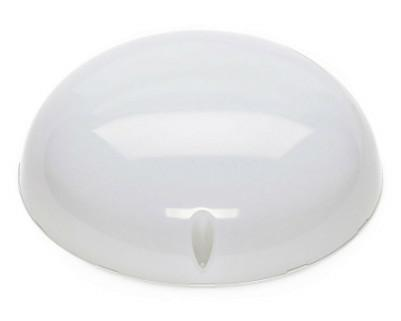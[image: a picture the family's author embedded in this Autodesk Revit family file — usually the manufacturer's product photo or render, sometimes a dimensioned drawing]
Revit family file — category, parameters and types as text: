
# Revit family: GALAD Находка LED
name_source: partatom
category: Осветительные приборы
revit_build: Autodesk Revit 2018 (Build: 20180423_1000(x64)
units: mm (PartAtom-declared; Revit-internal decimal feet)

## family parameters
Источник света = Да
Общий = Нет
Основа = Грань
При загрузке вырезать с полостями = Нет
Размер круглого соединителя = Использовать диаметр
Тип детали = Нормальный
Точка расчета площади = Нет

## types (1)
- GALAD Находка LED-9 ECO IP30
    ADSK_Версия Revit = 2018
    ADSK_Версия семейства = 1.01
    ADSK_Единица измерения = шт.
    ADSK_Классификация нагрузок = Освещение
    ADSK_Код изделия = 18158
    ADSK_Количество = 1
    ADSK_Количество фаз = 1
    ADSK_Коэффициент мощности = 0.95
    ADSK_Марка = GALAD Находка LED-9 ECO IP30
    ADSK_Масса = 0.2
    ADSK_Масса_Текст = 0.2
    ADSK_Наименование = GALAD Находка LED-9 ECO IP30
    ADSK_Наименование краткое = GALAD Находка LED-9 ECO IP30
    ADSK_Напряжение = 230 В
    ADSK_Номинальная мощность = 9 В·А
    ADSK_Обозначение = ГОСТ 15150-69
    ADSK_Полная мощность = 9 В·А
    ADSK_Размер_Высота = 53 мм
    ADSK_Размер_Длина = 174 мм
    ADSK_Размер_Ширина = 174 мм
    ADSK_Ток = 0 А
    ADSK_Энергоэффективность = 56 лм/Вт
    IP = 30
    URL = https://galad.ru
    Блок аварийного питания = Нет
    Видимая форма излучения при визуализации = Нет
    Возможный угол наклона = 0
    Группа модели = Светильники
    Диапазон цветовой температуры = 5028±283
    Изготовитель = АО «КАДОШКИНСКИЙ ЭЛЕКТРОТЕХНИЧЕСКИЙ ЗАВОД»
    Излучение по диаметру окружности = 610 мм
    Класс Защиты = 1
    Класс защиты от поражения электрическим током = 2
    Класс светораспределения = П
    Климатическая зона = УХЛ4
    Климатическое исполнение = 1…35 °С
    Коэффициент пульсации = менее 5%
    Материал корпуса = ПММА
    Материал рассеивателя = ПММА
    Неравномерность яркости = 0
    Область использования = ЖКХ
    Описание = Светодиодный светильник GALAD Находка LED укомплектован матовым рассеивателем для минимизации слепящего действия и встроенным блоком питания. Ударопрочное защитное стекло выполнено из светостабилизированного поликарбоната. Установка светильника возможна на стену или на потолок.
    Отметка по умолчанию = 1219 мм
    Полная установленная мощность = 9 В·А
    Световая отдача = 56
    Светофильтр = 16777215
    Смещение цветовой температуры при затухании лампы = <Нет>
    Снижение светового потока во время разгорания = не более 6%
    Срок службы = 12 лет
    Тип КСС = Косинусная
    Тип ПРА = ЭПРА
    Тип источника света = LED
    Тип монтажной поверхности = настенный
    Тип продукции = Светильник
    Тип устройства управления светодиодами = без управления
    Угол наклона = -90.00°
    Файл фотометрической сетки = GALAD nahodka LED-9 ECO IP30.IES
    Цветопередача = 80
    Частота = 50
